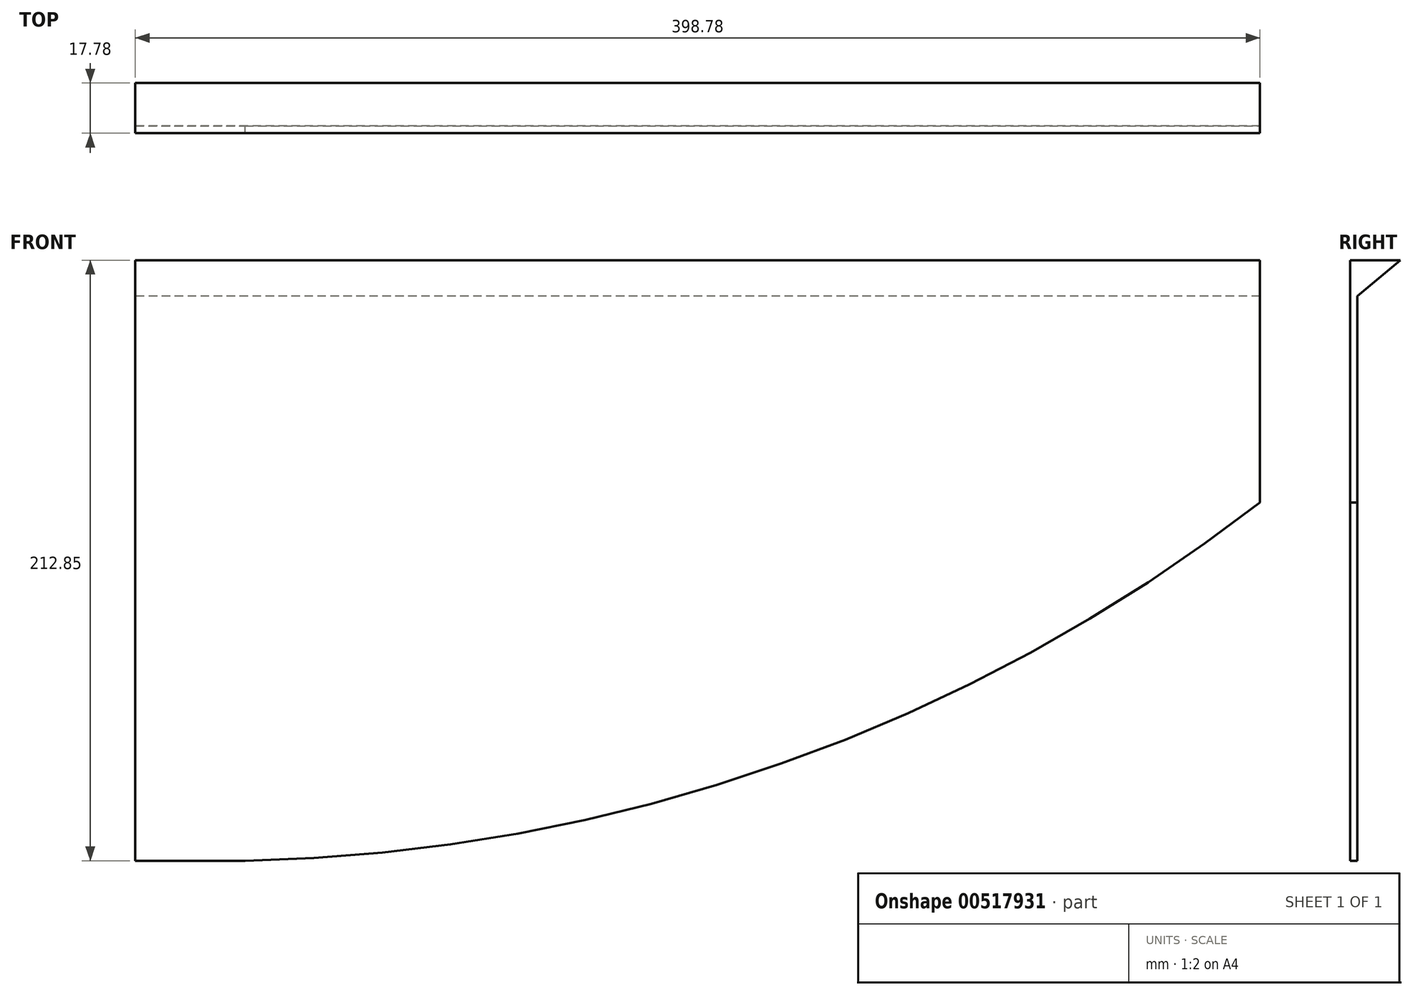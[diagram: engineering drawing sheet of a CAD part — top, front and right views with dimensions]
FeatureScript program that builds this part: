
annotation { "Feature Type Name" : "Feature", "Feature Type Description" : "" }
export const myFeature = defineFeature(function(context is Context, id is Id, definition is map)
    precondition{}
    {
        {
            var Q0;
            Q0=qCreatedBy(makeId("Front.planeOp"),FACE);
            var sketch = newSketch(context, id + "F0", { "sketchPlane" : qUnion([Q0])});
            skLineSegment(sketch, "E0", {"start": v(-188.26, -71.34) * mm, "end": v(210.52, -71.34) * mm});
            skLineSegment(sketch, "E1", {"start": v(210.52, -71.34) * mm, "end": v(210.52, -284.19) * mm});
            skLineSegment(sketch, "E2", {"start": v(-188.26, -139.4) * mm, "end": v(-188.26, -71.34) * mm});
            skPoint(sketch, "E3", {"position": v(-172.26, -284.19) * mm});
            skPoint(sketch, "E4", {"position": v(210.52, -157.19) * mm});
            skArc(sketch, "E5", {"start": v(-172.26, -284.19) * mm, "mid": v(30, -253.47) * mm, "end": v(210.52, -157.19) * mm});
            skLineSegment(sketch, "E6", {"start": v(-188.26, -139.4) * mm, "end": v(-188.26, -284.19) * mm});
            skLineSegment(sketch, "E7", {"start": v(-188.26, -284.19) * mm, "end": v(210.52, -284.19) * mm});
            skSolve(sketch);
        }
        {
            var Q0;
            {var subQ1=sQuery(id+"F0.wireOp",EDGE,"E0");Q0=makeQuery(id+"F0.imprint","IMPRINT",FACE,{"disambiguationData":[TD([[makeQuery(id+"F0.imprint","IMPRINT",EDGE,{"derivedFrom":subQ1}),-1.0]])]});}
            extrude(context, id + "F1", {"entities" : qUnion([Q0]), "depth" : 2.54 * mm, "offsetDistance" : 25.4 * mm});
        }
        {
            var Q0;
            Q0=makeQuery(id+"F1.opExtrude","CAP_FACE",FACE,{"disambiguationData":[OSD([sQuery(id+"F0.wireOp",EDGE,"E0"),sQuery(id+"F0.wireOp",EDGE,"E1"),sQuery(id+"F0.wireOp",EDGE,"E2"),sQuery(id+"F0.wireOp",EDGE,"E5"),sQuery(id+"F0.wireOp",EDGE,"E6"),sQuery(id+"F0.wireOp",EDGE,"E7")])],"isStart":true});
            var sketch = newSketch(context, id + "F2", { "sketchPlane" : qUnion([Q0])});
            skLineSegment(sketch, "E8.bottom", {"start": v(-210.52, -71.34) * mm, "end": v(188.26, -71.34) * mm});
            skLineSegment(sketch, "E8.top", {"start": v(-210.52, -84.04) * mm, "end": v(188.26, -84.04) * mm});
            skLineSegment(sketch, "E8.left", {"start": v(-210.52, -71.34) * mm, "end": v(-210.52, -84.04) * mm});
            skLineSegment(sketch, "E8.right", {"start": v(188.26, -71.34) * mm, "end": v(188.26, -84.04) * mm});
            skSolve(sketch);
        }
        {
            var Q0;
            Q0=makeQuery(id+"F2.imprint","IMPRINT",FACE,{"disambiguationData":[TD([[makeQuery(id+"F2.imprint","IMPRINT",EDGE,{"derivedFrom":sQuery(id+"F2.wireOp",EDGE,"E8.bottom")}),1.0]])]});
            extrude(context, id + "F3", {"entities" : qUnion([Q0]), "operationType" : NewBodyOperationType.ADD, "depth" : 15.24 * mm, "offsetDistance" : 25.4 * mm});
        }
        {
            var Q0;
            Q0=makeQuery(id+"F3.boolean.opBoolean","MERGE",FACE,{"derivedFrom":[makeQuery(id+"F1.opExtrude","SWEPT_FACE",FACE,{"disambiguationData":[OSD([sQuery(id+"F0.wireOp",EDGE,"E1")])]}),makeQuery(id+"F3.opExtrude","SWEPT_FACE",FACE,{"disambiguationData":[OSD([sQuery(id+"F2.wireOp",EDGE,"E8.left")])]})]});
            var sketch = newSketch(context, id + "F4", { "sketchPlane" : qUnion([Q0])});
            skLineSegment(sketch, "E9", {"start": v(0, -84.04) * mm, "end": v(15.24, -71.34) * mm});
            skSolve(sketch);
        }
        {
            var Q0;
            Q0=makeQuery(id+"F4.imprint","IMPRINT",FACE,{"disambiguationData":[TD([[makeQuery(id+"F4.imprint","IMPRINT",EDGE,{"derivedFrom":sQuery(id+"F4.wireOp",EDGE,"E9")}),-1.0]])]});
            extrude(context, id + "F5", {"entities" : qUnion([Q0]), "operationType" : NewBodyOperationType.REMOVE, "oppositeDirection" : true, "depth" : 406.4 * mm, "offsetDistance" : 25.4 * mm});
        }
    });
